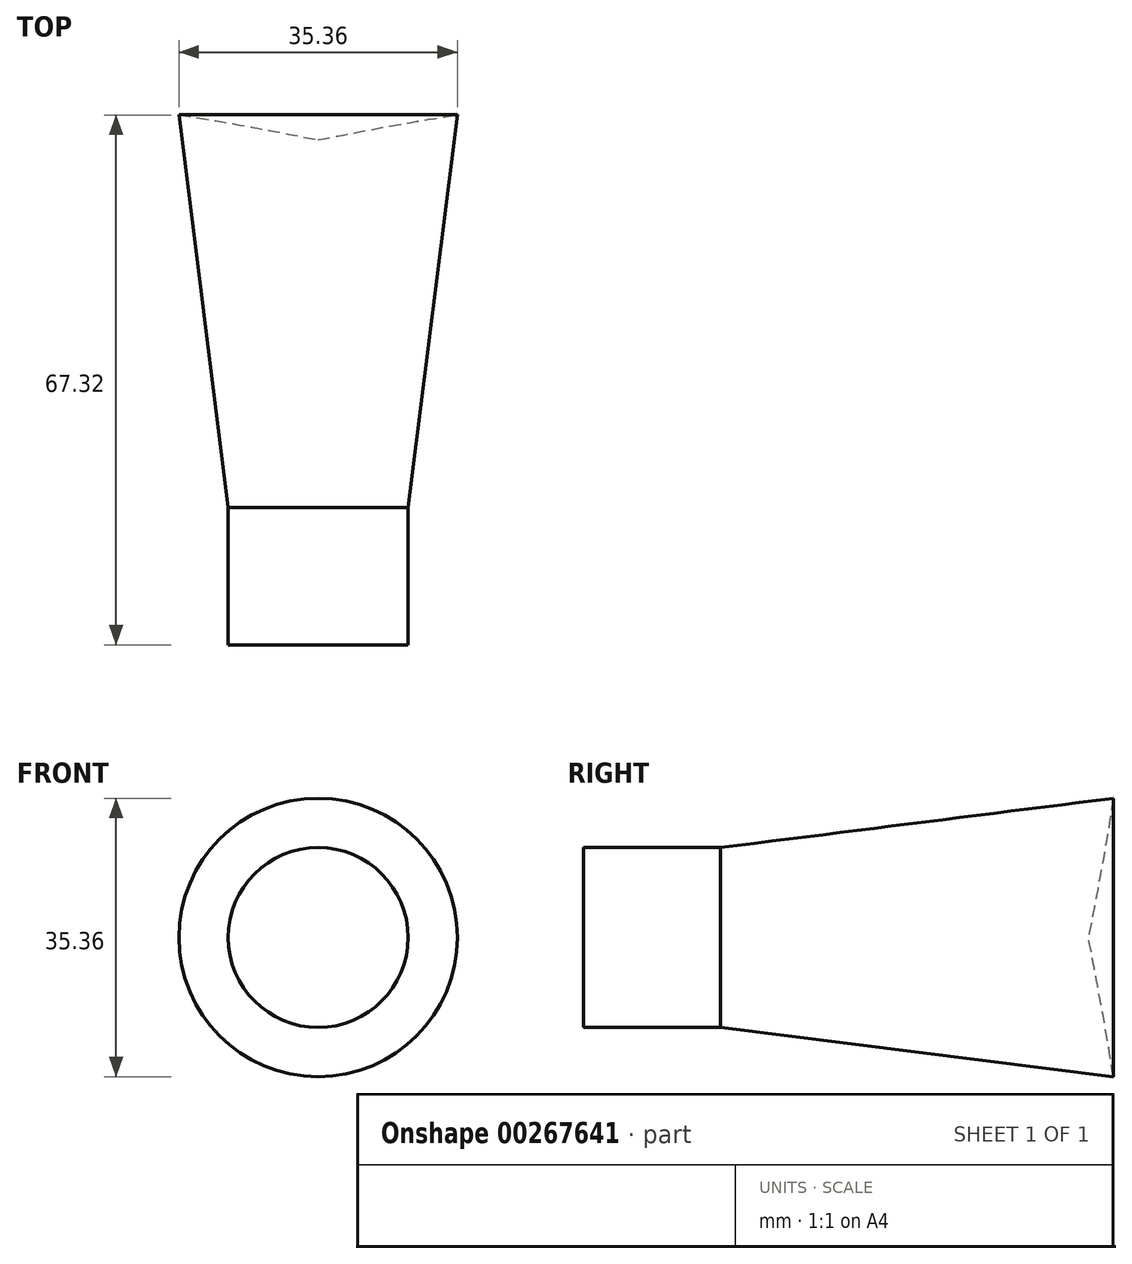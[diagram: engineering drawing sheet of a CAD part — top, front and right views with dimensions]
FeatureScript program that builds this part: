
annotation { "Feature Type Name" : "Feature", "Feature Type Description" : "" }
export const myFeature = defineFeature(function(context is Context, id is Id, definition is map)
    precondition{}
    {
        {
            var Q0;
            Q0=qCreatedBy(makeId("Top.planeOp"),FACE);
            var sketch = newSketch(context, id + "F0", { "sketchPlane" : qUnion([Q0])});
            skFitSpline(sketch, "E0", {"points": [v(0, 19.7) * mm, v(38.03, 20.5) * mm, v(27, -10.84) * mm, v(24.63, -30.94) * mm, v(0, -32.32) * mm], "startDerivative": vector(184.4, 35.83) * mm, "endDerivative": vector(-137.15, 15.74) * mm});
            skLineSegment(sketch, "E1", {"start": v(0, 19.7) * mm, "end": v(0, -32.32) * mm});
            skLineSegment(sketch, "E2", {"start": v(17.72, 23.15) * mm, "end": v(10.61, -33.54) * mm});
            skSolve(sketch);
        }
        {
            var Q0;
            {var subQ0=sQuery(id+"F0.wireOp",EDGE,"E2");var subQ1=sQuery(id+"F0.wireOp",EDGE,"E0");var subQ2=makeQuery(id+"F0.imprint","INTERSECT",VERTEX,{"disambiguationData":[OD(0.0)],"derivedFrom":[subQ1,subQ0]});Q0=makeQuery(id+"F0.imprint","IMPRINT",FACE,{"disambiguationData":[TD([[makeQuery(id+"F0.imprint","IMPRINT",EDGE,{"disambiguationData":[TD([[subQ2,-1.0]])],"derivedFrom":subQ1}),-1.0]])]});}
            var Q1;
            Q1=sQuery(id+"F0.wireOp",EDGE,"E1");
            revolve(context, id + "F1", {"entities" : qUnion([Q0]), "axis" : qUnion([Q1]), "revolveType" : RevolveType.FULL});
        }
        {
            var Q0;
            Q0=qCreatedBy(makeId("Front.planeOp"),FACE);
            var sketch = newSketch(context, id + "F2", { "sketchPlane" : qUnion([Q0])});
            skCircle(sketch, "E3", {"center": v(0, 0) * mm, "radius": 11.43 * mm});
            skSolve(sketch);
        }
        {
            var Q0;
            Q0 = qSketchRegion(id + "F2", true);
            extrude(context, id + "F3", {"entities" : qUnion([Q0]), "operationType" : NewBodyOperationType.ADD, "depth" : 44.45 * mm});
        }
    });
